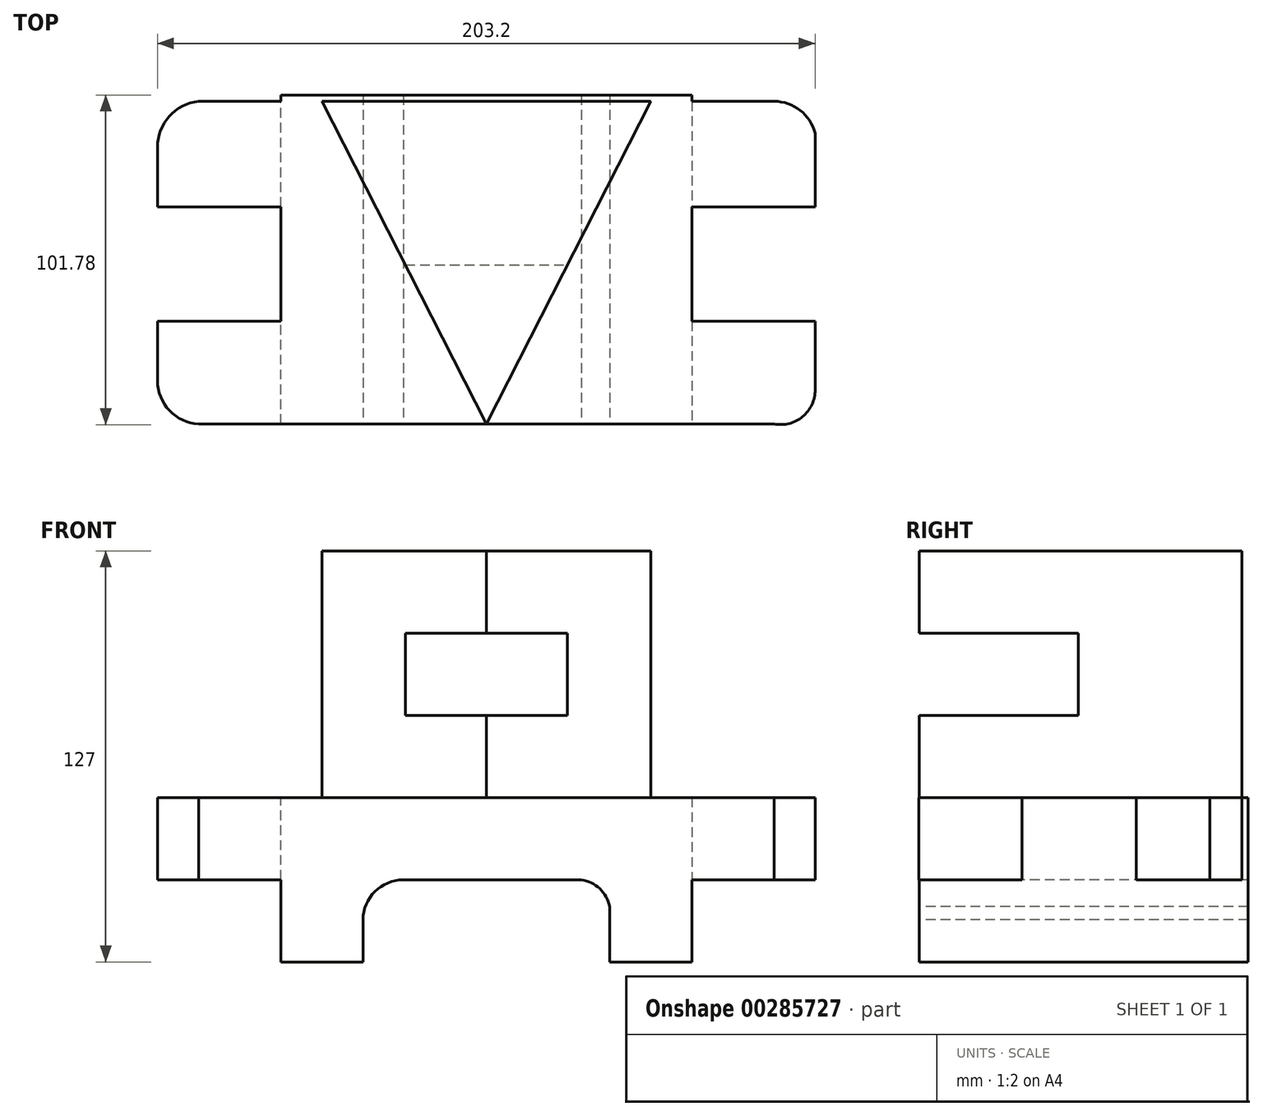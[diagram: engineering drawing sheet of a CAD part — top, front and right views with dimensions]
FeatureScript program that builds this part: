
annotation { "Feature Type Name" : "Feature", "Feature Type Description" : "" }
export const myFeature = defineFeature(function(context is Context, id is Id, definition is map)
    precondition{}
    {
        {
            var Q0;
            Q0=qCreatedBy(makeId("Top.planeOp"),FACE);
            var sketch = newSketch(context, id + "F0", { "sketchPlane" : qUnion([Q0])});
            skLineSegment(sketch, "E0", {"start": v(-50.8, 50.53) * mm, "end": v(50.8, 50.53) * mm});
            skLineSegment(sketch, "E1", {"start": v(50.8, 50.53) * mm, "end": v(0, -49.17) * mm});
            skLineSegment(sketch, "E2", {"start": v(0, -49.17) * mm, "end": v(-50.8, 50.53) * mm});
            skSolve(sketch);
        }
        {
            var Q0;
            Q0=makeQuery(id+"F0.imprint","IMPRINT",FACE,{"disambiguationData":[TD([[makeQuery(id+"F0.imprint","IMPRINT",EDGE,{"derivedFrom":sQuery(id+"F0.wireOp",EDGE,"E0")}),-1.0]])]});
            extrude(context, id + "F1", {"entities" : qUnion([Q0]), "depth" : 25.4 * mm});
        }
        {
            var Q0;
            Q0=makeQuery(id+"F1.opExtrude","CAP_FACE",FACE,{"disambiguationData":[OSD([sQuery(id+"F0.wireOp",EDGE,"E0"),sQuery(id+"F0.wireOp",EDGE,"E1"),sQuery(id+"F0.wireOp",EDGE,"E2")])],"isStart":true});
            var sketch = newSketch(context, id + "F2", { "sketchPlane" : qUnion([Q0])});
            skLineSegment(sketch, "E3", {"start": v(-25.05, 0) * mm, "end": v(0, 0) * mm});
            skLineSegment(sketch, "E4", {"start": v(0, 0) * mm, "end": v(25.05, 0) * mm});
            skLineSegment(sketch, "E5", {"start": v(25.05, 0) * mm, "end": v(0, 49.17) * mm});
            skLineSegment(sketch, "E6", {"start": v(0, 49.17) * mm, "end": v(-25.05, 0) * mm});
            skLineSegment(sketch, "E7", {"start": v(-25.05, 0) * mm, "end": v(-50.8, -50.53) * mm});
            skLineSegment(sketch, "E8", {"start": v(-50.8, -50.53) * mm, "end": v(50.8, -50.53) * mm});
            skLineSegment(sketch, "E9", {"start": v(50.8, -50.53) * mm, "end": v(25.05, 0) * mm});
            skSolve(sketch);
        }
        {
            var Q0;
            Q0=makeQuery(id+"F2.imprint","IMPRINT",FACE,{"disambiguationData":[TD([[makeQuery(id+"F2.imprint","IMPRINT",EDGE,{"derivedFrom":sQuery(id+"F2.wireOp",EDGE,"E3")}),-1.0]])]});
            extrude(context, id + "F3", {"entities" : qUnion([Q0]), "operationType" : NewBodyOperationType.ADD, "depth" : 25.4 * mm});
        }
        {
            var Q0;
            Q0=makeQuery(id+"F3.opExtrude","CAP_FACE",FACE,{"disambiguationData":[OSD([sQuery(id+"F2.wireOp",EDGE,"E3"),sQuery(id+"F2.wireOp",EDGE,"E4"),sQuery(id+"F2.wireOp",EDGE,"E7"),sQuery(id+"F2.wireOp",EDGE,"E8"),sQuery(id+"F2.wireOp",EDGE,"E9")])],"isStart":false});
            var sketch = newSketch(context, id + "F4", { "sketchPlane" : qUnion([Q0])});
            skLineSegment(sketch, "E10", {"start": v(-25.05, 0) * mm, "end": v(-50.8, -50.53) * mm});
            skLineSegment(sketch, "E11", {"start": v(-50.8, -50.53) * mm, "end": v(50.8, -50.53) * mm});
            skLineSegment(sketch, "E12", {"start": v(50.8, -50.53) * mm, "end": v(25.05, 0) * mm});
            skLineSegment(sketch, "E13", {"start": v(25.05, 0) * mm, "end": v(0, 49.17) * mm});
            skPoint(sketch, "E13.endSnap0", {"position": v(0, 0) * mm});
            skLineSegment(sketch, "E14", {"start": v(0, 49.17) * mm, "end": v(-25.05, 0) * mm});
            skSolve(sketch);
        }
        {
            var Q0;
            Q0=makeQuery(id+"F4.imprint","IMPRINT",FACE,{"disambiguationData":[TD([[makeQuery(id+"F4.imprint","IMPRINT",EDGE,{"derivedFrom":sQuery(id+"F4.wireOp",EDGE,"E10")}),1.0]])]});
            extrude(context, id + "F5", {"entities" : qUnion([Q0]), "operationType" : NewBodyOperationType.ADD, "depth" : 25.4 * mm});
        }
        {
            var Q0;
            Q0=makeQuery(id+"F4.imprint","IMPRINT",FACE,{"disambiguationData":[TD([[makeQuery(id+"F4.imprint","IMPRINT",EDGE,{"derivedFrom":sQuery(id+"F4.wireOp",EDGE,"E13")}),1.0]])]});
            extrude(context, id + "F6", {"entities" : qUnion([Q0]), "operationType" : NewBodyOperationType.ADD, "depth" : 25.4 * mm});
        }
        {
            var Q0;
            {var subQ0=sQuery(id+"F2.wireOp",EDGE,"E4");var subQ1=sQuery(id+"F2.wireOp",EDGE,"E3");Q0=makeQuery(id+"F6.boolean.opBoolean","MERGE",FACE,{"derivedFrom":[makeQuery(id+"F5.opExtrude","CAP_FACE",FACE,{"disambiguationData":[OSD([subQ1,subQ0,sQuery(id+"F4.wireOp",EDGE,"E10"),sQuery(id+"F4.wireOp",EDGE,"E11"),sQuery(id+"F4.wireOp",EDGE,"E12")])],"isStart":false}),makeQuery(id+"F6.opExtrude","CAP_FACE",FACE,{"disambiguationData":[OSD([subQ1,subQ0,sQuery(id+"F4.wireOp",EDGE,"E13"),sQuery(id+"F4.wireOp",EDGE,"E14")])],"isStart":false})]});}
            var sketch = newSketch(context, id + "F7", { "sketchPlane" : qUnion([Q0])});
            skPoint(sketch, "E15.endSnap0", {"position": v(0, -50.53) * mm});
            skLineSegment(sketch, "E16", {"start": v(0, -50.53) * mm, "end": v(-88.9, -50.53) * mm});
            skLineSegment(sketch, "E17", {"start": v(0, -50.53) * mm, "end": v(88.9, -50.53) * mm});
            skLineSegment(sketch, "E18", {"start": v(-101.6, -36.32) * mm, "end": v(-101.6, -17.89) * mm});
            skLineSegment(sketch, "E19", {"start": v(-101.6, -17.89) * mm, "end": v(-63.5, -17.89) * mm});
            skLineSegment(sketch, "E20", {"start": v(-63.5, -17.89) * mm, "end": v(-63.5, 17.42) * mm});
            skLineSegment(sketch, "E21", {"start": v(-63.5, 17.42) * mm, "end": v(-101.6, 17.42) * mm});
            skLineSegment(sketch, "E22", {"start": v(-101.6, 17.42) * mm, "end": v(-101.6, 35.78) * mm});
            skLineSegment(sketch, "E23", {"start": v(-88.9, 49.17) * mm, "end": v(0, 49.17) * mm});
            skLineSegment(sketch, "E24", {"start": v(0, 49.17) * mm, "end": v(92.84, 49.17) * mm});
            skLineSegment(sketch, "E25", {"start": v(101.6, 38.62) * mm, "end": v(101.6, 17.42) * mm});
            skLineSegment(sketch, "E26", {"start": v(101.6, 17.42) * mm, "end": v(63.5, 17.42) * mm});
            skLineSegment(sketch, "E27", {"start": v(63.5, 17.42) * mm, "end": v(63.5, -17.89) * mm});
            skLineSegment(sketch, "E28", {"start": v(63.5, -17.89) * mm, "end": v(101.6, -17.89) * mm});
            skLineSegment(sketch, "E29", {"start": v(101.6, -17.89) * mm, "end": v(101.6, -40.64) * mm});
            skArc(sketch, "E30", {"start": v(-88.9, 49.17) * mm, "mid": v(-97.92, 45) * mm, "end": v(-101.6, 35.78) * mm});
            skArc(sketch, "E31", {"start": v(-101.6, -36.32) * mm, "mid": v(-97.96, -45.85) * mm, "end": v(-88.9, -50.53) * mm});
            skPoint(sketch, "E32.orphan", {"position": v(-101.6, 49.17) * mm});
            skArc(sketch, "E33", {"start": v(101.6, 38.62) * mm, "mid": v(97.73, 46.87) * mm, "end": v(88.9, 49.17) * mm});
            skArc(sketch, "E34", {"start": v(88.9, -50.53) * mm, "mid": v(96.95, -47.77) * mm, "end": v(101.6, -40.64) * mm});
            skPoint(sketch, "E35.orphan", {"position": v(101.6, 49.17) * mm});
            skPoint(sketch, "E36.orphan", {"position": v(101.6, -50.53) * mm});
            skPoint(sketch, "E37.orphan", {"position": v(101.6, -34.2) * mm});
            skSolve(sketch);
        }
        {
            var Q0;
            {var subQ0=sQuery(id+"F7.wireOp",EDGE,"E33");var subQ1=sQuery(id+"F7.wireOp",EDGE,"E24");var subQ2=makeQuery(id+"F7.imprint","INTERSECT",VERTEX,{"disambiguationData":[OD(0.0)],"derivedFrom":[subQ1,subQ0]});Q0=makeQuery(id+"F7.imprint","IMPRINT",FACE,{"disambiguationData":[TD([[makeQuery(id+"F7.imprint","IMPRINT",EDGE,{"disambiguationData":[TD([[subQ2,1.0]])],"derivedFrom":subQ1}),1.0]])]});}
            var Q1;
            {var subQ1=makeQuery(id+"F6.boolean.opBoolean","MERGE",EDGE,{"derivedFrom":[makeQuery(id+"F5.opExtrude","CAP_EDGE",EDGE,{"disambiguationData":[OSD([sQuery(id+"F4.wireOp",EDGE,"E10")])],"isStart":false}),makeQuery(id+"F6.opExtrude","CAP_EDGE",EDGE,{"disambiguationData":[OSD([sQuery(id+"F4.wireOp",EDGE,"E14")])],"isStart":false})]});Q1=makeQuery(id+"F7.imprint","IMPRINT",FACE,{"disambiguationData":[TD([[makeQuery(id+"F7.imprint","IMPRINT",EDGE,{"derivedFrom":subQ1}),1.0]])]});}
            var Q2;
            {var subQ3=sQuery(id+"F7.wireOp",EDGE,"E25");Q2=makeQuery(id+"F7.imprint","IMPRINT",FACE,{"disambiguationData":[TD([[makeQuery(id+"F7.imprint","IMPRINT",EDGE,{"derivedFrom":subQ3}),-1.0]])]});}
            extrude(context, id + "F8", {"entities" : qUnion([Q0, Q1, Q2]), "operationType" : NewBodyOperationType.ADD, "depth" : 25.4 * mm});
        }
        {
            var Q0;
            Q0=makeQuery(id+"F7.imprint","IMPRINT",FACE,{"disambiguationData":[TD([[makeQuery(id+"F7.imprint","IMPRINT",EDGE,{"derivedFrom":sQuery(id+"F7.wireOp",EDGE,"E18")}),-1.0]])]});
            extrude(context, id + "F9", {"entities" : qUnion([Q0]), "operationType" : NewBodyOperationType.ADD, "depth" : 25.4 * mm});
        }
        {
            var Q0;
            Q0=makeQuery(id+"F9.boolean.opBoolean","MERGE",FACE,{"derivedFrom":[makeQuery(id+"F8.opExtrude","SWEPT_FACE",FACE,{"disambiguationData":[OSD([sQuery(id+"F7.wireOp",EDGE,"E24")])]}),makeQuery(id+"F9.opExtrude","SWEPT_FACE",FACE,{"disambiguationData":[OSD([sQuery(id+"F7.wireOp",EDGE,"E23")])]})]});
            var sketch = newSketch(context, id + "F10", { "sketchPlane" : qUnion([Q0])});
            skLineSegment(sketch, "E38", {"start": v(-63.5, -76.2) * mm, "end": v(-63.5, -101.6) * mm});
            skLineSegment(sketch, "E39", {"start": v(-63.5, -101.6) * mm, "end": v(-38.1, -101.6) * mm});
            skLineSegment(sketch, "E40", {"start": v(-38.1, -101.6) * mm, "end": v(-38.1, -88.6) * mm});
            skLineSegment(sketch, "E41", {"start": v(-38.1, -76.2) * mm, "end": v(38.1, -76.2) * mm});
            skLineSegment(sketch, "E42", {"start": v(38.1, -84.46) * mm, "end": v(38.1, -101.6) * mm});
            skLineSegment(sketch, "E43", {"start": v(38.1, -101.6) * mm, "end": v(63.5, -101.6) * mm});
            skLineSegment(sketch, "E44", {"start": v(63.5, -101.6) * mm, "end": v(63.5, -76.2) * mm});
            skLineSegment(sketch, "E45", {"start": v(63.5, -76.2) * mm, "end": v(63.5, -50.8) * mm});
            skLineSegment(sketch, "E46", {"start": v(63.5, -50.8) * mm, "end": v(-63.5, -50.8) * mm});
            skLineSegment(sketch, "E47", {"start": v(-63.5, -50.8) * mm, "end": v(-63.5, -76.2) * mm});
            skArc(sketch, "E48", {"start": v(-25.42, -76.2) * mm, "mid": v(-34.44, -79.88) * mm, "end": v(-38.1, -88.9) * mm});
            skArc(sketch, "E49", {"start": v(38.1, -88.75) * mm, "mid": v(35.43, -79.36) * mm, "end": v(26.2, -76.2) * mm});
            skSolve(sketch);
        }
        {
            var Q0;
            Q0 = qSketchRegion(id + "F10", true);
            extrude(context, id + "F11", {"entities" : qUnion([Q0]), "operationType" : NewBodyOperationType.ADD, "oppositeDirection" : true, "depth" : 101.6 * mm});
        }
    });
